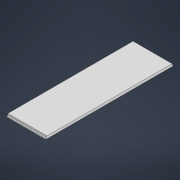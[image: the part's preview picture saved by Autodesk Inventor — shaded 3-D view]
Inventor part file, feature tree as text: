
AUTODESK INVENTOR PART (.ipt)
format: ipt  version: 2022 (Build 260153000, 153)  size: 105,472 bytes
history: native  units: mm
features: extrude x2, sketch x2
ambient origin geometry x8: Origin, YZ Plane, XZ Plane, XY Plane, X Axis, Y Axis, Z Axis, Center Point
bodies: 实体1 (feature_tree)
feature tree (4):
  extrude  "拉伸1"  Depth=92.2mm
  extrude  "拉伸2"  Depth=0.9mm
  sketch  "草图1"  dims[d0=28.2mm d1=92.2mm]
  sketch  "草图2"  dims[d2=1.8mm d3=0.0mm d4=0.9mm d5=0.64mm d6=0.9mm d7=0.0mm d8=0.0mm]
